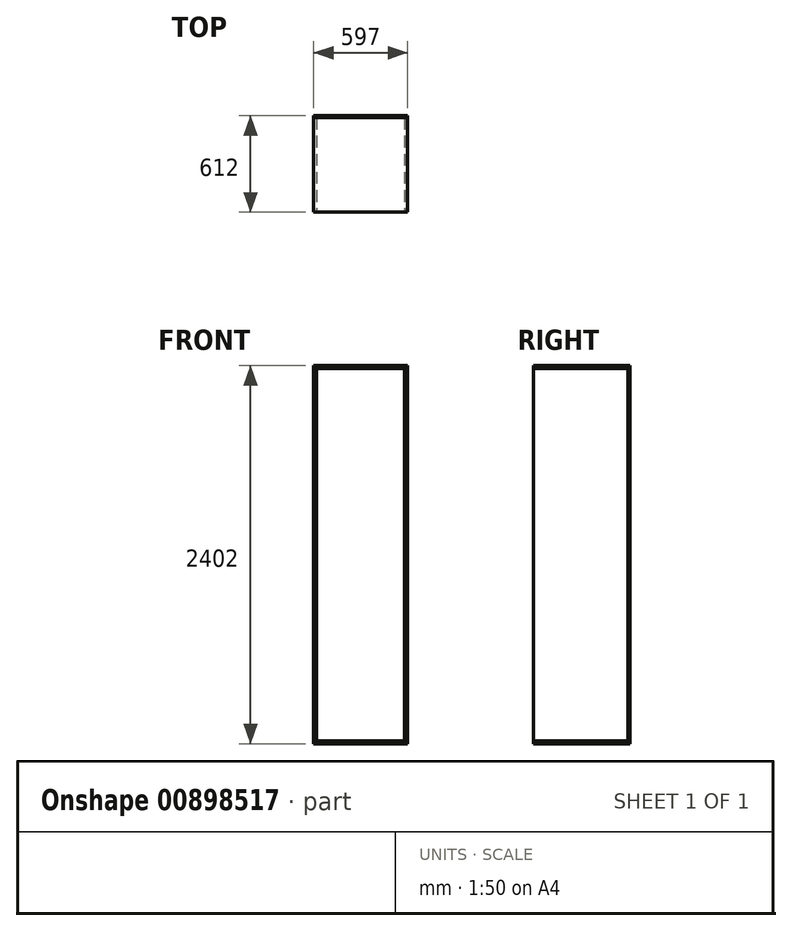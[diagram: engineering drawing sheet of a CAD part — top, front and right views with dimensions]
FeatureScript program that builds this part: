
annotation { "Feature Type Name" : "Feature", "Feature Type Description" : "" }
export const myFeature = defineFeature(function(context is Context, id is Id, definition is map)
    precondition{}
    {
        {
            var Q0;
            Q0=qCreatedBy(makeId("Top.planeOp"),FACE);
            var sketch = newSketch(context, id + "F0", { "sketchPlane" : qUnion([Q0])});
            skLineSegment(sketch, "E0.bottom", {"start": v(298.5, -300) * mm, "end": v(-298.5, -300) * mm});
            skLineSegment(sketch, "E0.top", {"start": v(298.5, 300) * mm, "end": v(-298.5, 300) * mm});
            skLineSegment(sketch, "E0.left", {"start": v(298.5, -300) * mm, "end": v(298.5, 300) * mm});
            skLineSegment(sketch, "E0.right", {"start": v(-298.5, -300) * mm, "end": v(-298.5, 300) * mm});
            skPoint(sketch, "E0.middle", {"position": v(0, 0) * mm});
            skSolve(sketch);
        }
        {
            assignVariable(context, id + "F1", {"name" : "thickness", "anyValue" : 19});
        }
        {
            var Q0;
            Q0=makeQuery(id+"F0.imprint","IMPRINT",FACE,{"disambiguationData":[TD([[makeQuery(id+"F0.imprint","IMPRINT",EDGE,{"derivedFrom":sQuery(id+"F0.wireOp",EDGE,"E0.bottom")}),-1.0]])]});
            extrude(context, id + "F2", {"entities" : qUnion([Q0]), "depth" : (getVariable(context, 'thickness')) * mm, "offsetDistance" : 25 * mm});
        }
        {
            assignVariable(context, id + "F3", {"name" : "height", "anyValue" : 2364});
        }
        {
            var Q0;
            Q0=makeQuery(id+"F2.opExtrude","CAP_FACE",FACE,{"disambiguationData":[OSD([sQuery(id+"F0.wireOp",EDGE,"E0.bottom"),sQuery(id+"F0.wireOp",EDGE,"E0.top"),sQuery(id+"F0.wireOp",EDGE,"E0.left"),sQuery(id+"F0.wireOp",EDGE,"E0.right")])],"isStart":false});
            var sketch = newSketch(context, id + "F4", { "sketchPlane" : qUnion([Q0])});
            skLineSegment(sketch, "E1.bottom", {"start": v(-298.5, 300) * mm, "end": v(-279.5, 300) * mm});
            skLineSegment(sketch, "E1.top", {"start": v(-298.5, -300) * mm, "end": v(-279.5, -300) * mm});
            skLineSegment(sketch, "E1.left", {"start": v(-298.5, 300) * mm, "end": v(-298.5, -300) * mm});
            skLineSegment(sketch, "E1.right", {"start": v(-279.5, 300) * mm, "end": v(-279.5, -300) * mm});
            skSolve(sketch);
        }
        {
            var Q0;
            Q0=makeQuery(id+"F4.imprint","IMPRINT",FACE,{"disambiguationData":[TD([[makeQuery(id+"F4.imprint","IMPRINT",EDGE,{"derivedFrom":sQuery(id+"F4.wireOp",EDGE,"E1.bottom")}),1.0]])]});
            extrude(context, id + "F5", {"entities" : qUnion([Q0]), "depth" : (getVariable(context, 'height')) * mm, "offsetDistance" : 25 * mm});
        }
        {
            var Q0;
            Q0=makeQuery(id+"F2.opExtrude","CAP_FACE",FACE,{"disambiguationData":[OSD([sQuery(id+"F0.wireOp",EDGE,"E0.bottom"),sQuery(id+"F0.wireOp",EDGE,"E0.top"),sQuery(id+"F0.wireOp",EDGE,"E0.left"),sQuery(id+"F0.wireOp",EDGE,"E0.right")])],"isStart":false});
            var sketch = newSketch(context, id + "F6", { "sketchPlane" : qUnion([Q0])});
            skLineSegment(sketch, "E2.bottom", {"start": v(298.5, 300) * mm, "end": v(279.5, 300) * mm});
            skLineSegment(sketch, "E2.top", {"start": v(298.5, -300) * mm, "end": v(279.5, -300) * mm});
            skLineSegment(sketch, "E2.left", {"start": v(298.5, 300) * mm, "end": v(298.5, -300) * mm});
            skLineSegment(sketch, "E2.right", {"start": v(279.5, 300) * mm, "end": v(279.5, -300) * mm});
            skSolve(sketch);
        }
        {
            var Q0;
            Q0=makeQuery(id+"F6.imprint","IMPRINT",FACE,{"disambiguationData":[TD([[makeQuery(id+"F6.imprint","IMPRINT",EDGE,{"derivedFrom":sQuery(id+"F6.wireOp",EDGE,"E2.bottom")}),1.0]])]});
            extrude(context, id + "F7", {"entities" : qUnion([Q0]), "depth" : (getVariable(context, 'height')) * mm, "offsetDistance" : 25 * mm});
        }
        {
            var Q0;
            Q0=makeQuery(id+"F5.opExtrude","CAP_FACE",FACE,{"disambiguationData":[OSD([sQuery(id+"F4.wireOp",EDGE,"E1.bottom"),sQuery(id+"F4.wireOp",EDGE,"E1.top"),sQuery(id+"F4.wireOp",EDGE,"E1.left"),sQuery(id+"F4.wireOp",EDGE,"E1.right")])],"isStart":false});
            var sketch = newSketch(context, id + "F8", { "sketchPlane" : qUnion([Q0])});
            skLineSegment(sketch, "E3.bottom", {"start": v(-298.5, 300) * mm, "end": v(298.5, 300) * mm});
            skLineSegment(sketch, "E3.top", {"start": v(-298.5, -300) * mm, "end": v(298.5, -300) * mm});
            skLineSegment(sketch, "E3.left", {"start": v(-298.5, 300) * mm, "end": v(-298.5, -300) * mm});
            skLineSegment(sketch, "E3.right", {"start": v(298.5, 300) * mm, "end": v(298.5, -300) * mm});
            skSolve(sketch);
        }
        {
            var Q0;
            {var subQ2=sQuery(id+"F8.wireOp",EDGE,"E3.right");Q0=makeQuery(id+"F8.imprint","IMPRINT",FACE,{"disambiguationData":[TD([[makeQuery(id+"F8.imprint","IMPRINT",EDGE,{"derivedFrom":subQ2}),-1.0]])]});}
            var Q1;
            {var subQ0=sQuery(id+"F8.wireOp",EDGE,"E3.left");Q1=makeQuery(id+"F8.imprint","IMPRINT",FACE,{"disambiguationData":[TD([[makeQuery(id+"F8.imprint","IMPRINT",EDGE,{"derivedFrom":subQ0}),-1.0]])]});}
            extrude(context, id + "F9", {"entities" : qUnion([Q0, Q1]), "depth" : (getVariable(context, 'thickness')) * mm, "offsetDistance" : 25 * mm});
        }
        {
            var Q0;
            Q0=makeQuery(id+"F9.opExtrude","SWEPT_FACE",FACE,{"disambiguationData":[OSD([sQuery(id+"F8.wireOp",EDGE,"E3.bottom")])]});
            var sketch = newSketch(context, id + "F10", { "sketchPlane" : qUnion([Q0])});
            skLineSegment(sketch, "E4.bottom", {"start": v(-298.5, 2402) * mm, "end": v(298.5, 2402) * mm});
            skLineSegment(sketch, "E4.top", {"start": v(-298.5, 0) * mm, "end": v(298.5, 0) * mm});
            skLineSegment(sketch, "E4.left", {"start": v(-298.5, 2402) * mm, "end": v(-298.5, 0) * mm});
            skLineSegment(sketch, "E4.right", {"start": v(298.5, 2402) * mm, "end": v(298.5, 0) * mm});
            skSolve(sketch);
        }
        {
            assignVariable(context, id + "F11", {"name" : "back", "anyValue" : 12});
        }
        {
            var Q0;
            {var subQ0=sQuery(id+"F10.wireOp",EDGE,"E4.top");Q0=makeQuery(id+"F10.imprint","IMPRINT",FACE,{"disambiguationData":[TD([[makeQuery(id+"F10.imprint","IMPRINT",EDGE,{"derivedFrom":subQ0}),1.0]])]});}
            var Q1;
            {var subQ0=sQuery(id+"F10.wireOp",EDGE,"E4.bottom");Q1=makeQuery(id+"F10.imprint","IMPRINT",FACE,{"disambiguationData":[TD([[makeQuery(id+"F10.imprint","IMPRINT",EDGE,{"derivedFrom":subQ0}),1.0]])]});}
            extrude(context, id + "F12", {"entities" : qUnion([Q0, Q1]), "depth" : (getVariable(context, 'back')) * mm, "offsetDistance" : 25 * mm});
        }
    });
